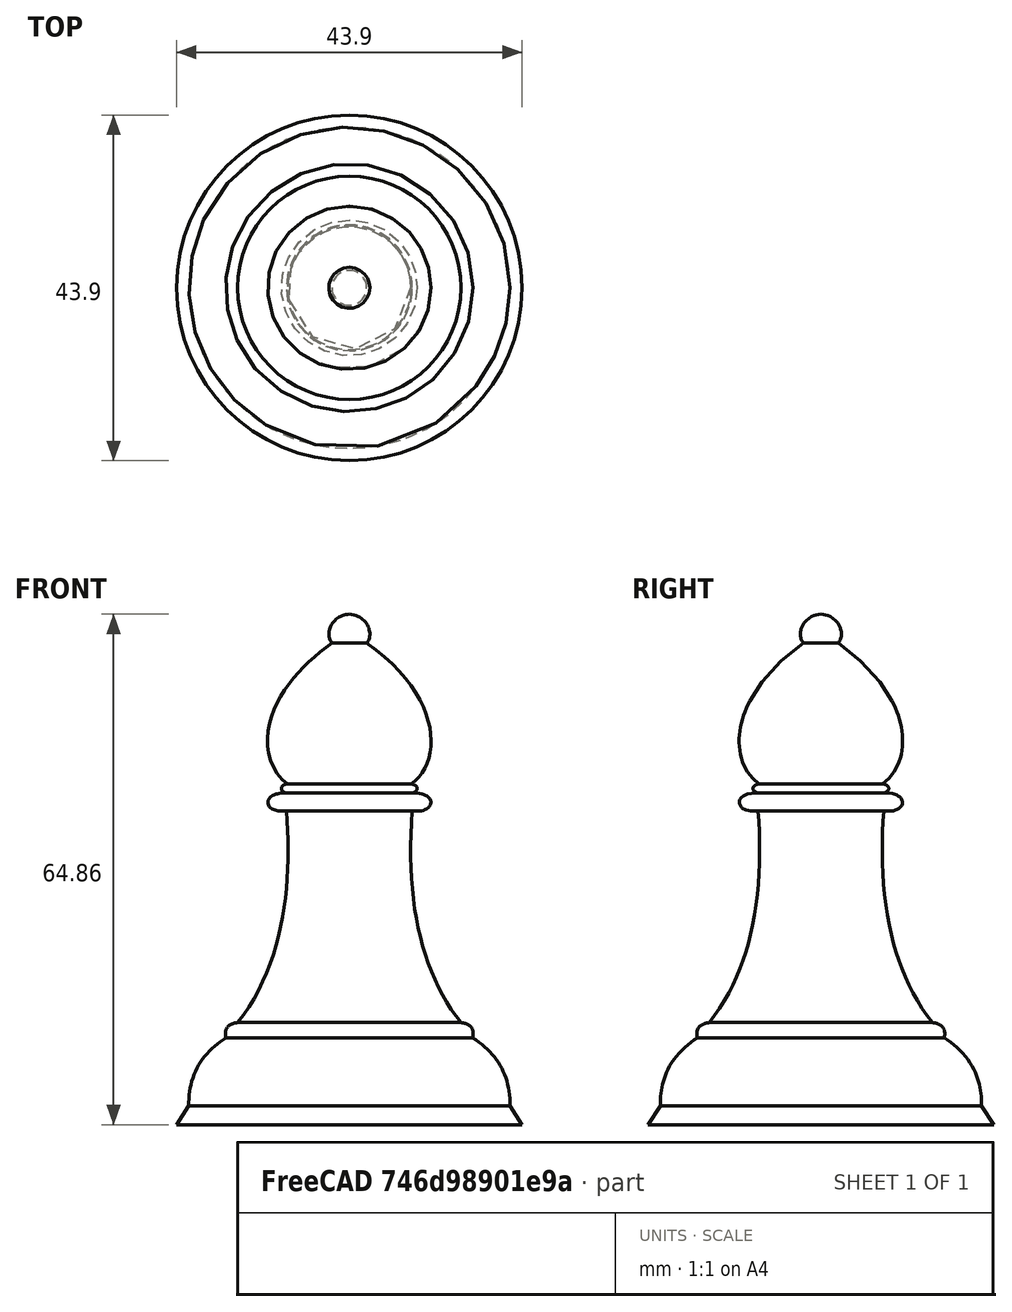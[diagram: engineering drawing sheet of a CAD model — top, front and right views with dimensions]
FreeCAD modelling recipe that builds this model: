
FCSTD DOCUMENT  (FreeCAD 0.20R29177 +426 (Git))
Label: alfil
License: Creative Commons Attribution-ShareAlike
LicenseURL: http://creativecommons.org/licenses/by-sa/4.0/
objects: Sketcher::SketchObject×1, Part::Revolution×1
note: 2 computed .brp shape members not serialized (recipe doc carries the construction recipe); baked Part::Feature solids carry a one-line shape summary decoded from their .brp

FEATURE [Sketcher::SketchObject] Sketch
  FullyConstrained = false
  Placement = pos=(0,0,0) rot=(1,0,0;1.5708rad)
  sketch-geometry (49):
    g0: LineSegment StartX=0 StartY=0 StartZ=0 EndX=21.9512 EndY=0 EndZ=0
    g1: LineSegment StartX=21.9512 StartY=0 StartZ=0 EndX=20.4013 EndY=2.40979 EndZ=0
    g2: Circle CenterX=20.4013 CenterY=2.40979 CenterZ=0 NormalX=0 NormalY=0 NormalZ=1 AngleXU=0 Radius=1
    g3: Circle CenterX=20.4986 CenterY=7.95886 CenterZ=0 NormalX=0 NormalY=0 NormalZ=1 AngleXU=0 Radius=1
    g4: Circle CenterX=15.6707 CenterY=11.0375 CenterZ=0 NormalX=0 NormalY=0 NormalZ=1 AngleXU=0 Radius=1
    g5: BSplineCurve PolesCount=3 KnotsCount=2 Degree=2 IsPeriodic=0
    g6: GeomPoint X=20.4013 Y=2.40979 Z=0
    g7: GeomPoint X=15.6707 Y=11.0375 Z=0
    g8: Circle CenterX=15.6707 CenterY=11.0375 CenterZ=0 NormalX=0 NormalY=0 NormalZ=1 AngleXU=0 Radius=1
    g9: Circle CenterX=16.0644 CenterY=12.7435 CenterZ=0 NormalX=0 NormalY=0 NormalZ=1 AngleXU=0 Radius=1
    g10: Circle CenterX=14.1834 CenterY=12.9622 CenterZ=0 NormalX=0 NormalY=0 NormalZ=1 AngleXU=0 Radius=1
    g11: BSplineCurve PolesCount=3 KnotsCount=2 Degree=2 IsPeriodic=0
    g12: GeomPoint X=15.6707 Y=11.0375 Z=0
    g13: GeomPoint X=14.1834 Y=12.9622 Z=0
    g14: Circle CenterX=14.1834 CenterY=12.9622 CenterZ=0 NormalX=0 NormalY=0 NormalZ=1 AngleXU=0 Radius=1
    g15: Circle CenterX=6.6662 CenterY=22.465 CenterZ=0 NormalX=0 NormalY=0 NormalZ=1 AngleXU=0 Radius=1
    g16: Circle CenterX=7.98136 CenterY=39.8756 CenterZ=0 NormalX=0 NormalY=0 NormalZ=1 AngleXU=0 Radius=1
    g17: BSplineCurve PolesCount=3 KnotsCount=2 Degree=2 IsPeriodic=0
    g18: GeomPoint X=14.1834 Y=12.9622 Z=0
    g19: GeomPoint X=7.98136 Y=39.8756 Z=0
    g20-g23: Circle x4 (B-spline internal-alignment scaffolding for g24; pole/knot coordinates omitted)
    g24: BSplineCurve PolesCount=4 KnotsCount=2 Degree=3 IsPeriodic=0
    g25: GeomPoint X=7.98136 Y=39.8756 Z=0
    g26: GeomPoint X=7.9451 Y=42.1219 Z=0
    g27: Circle CenterX=7.9451 CenterY=42.1219 CenterZ=0 NormalX=0 NormalY=0 NormalZ=1 AngleXU=0 Radius=1
    g28: Circle CenterX=9.0659 CenterY=42.3703 CenterZ=0 NormalX=0 NormalY=0 NormalZ=1 AngleXU=0 Radius=1
    g29: Circle CenterX=8.64352 CenterY=43.2767 CenterZ=0 NormalX=0 NormalY=0 NormalZ=1 AngleXU=0 Radius=1
    g30: Circle CenterX=7.84367 CenterY=43.2664 CenterZ=0 NormalX=0 NormalY=0 NormalZ=1 AngleXU=0 Radius=1
    g31: BSplineCurve PolesCount=4 KnotsCount=2 Degree=3 IsPeriodic=0
    g32: GeomPoint X=7.9451 Y=42.1219 Z=0
    g33: GeomPoint X=7.84367 Y=43.2664 Z=0
    g34: Circle CenterX=7.84367 CenterY=43.2664 CenterZ=0 NormalX=0 NormalY=0 NormalZ=1 AngleXU=0 Radius=1
    g35: Circle CenterX=12.0104 CenterY=46.2983 CenterZ=0 NormalX=0 NormalY=0 NormalZ=1 AngleXU=0 Radius=1
    g36: Circle CenterX=11.6605 CenterY=54.5658 CenterZ=0 NormalX=0 NormalY=0 NormalZ=1 AngleXU=0 Radius=1
    g37: Circle CenterX=2.21194 CenterY=61.171 CenterZ=0 NormalX=0 NormalY=0 NormalZ=1 AngleXU=0 Radius=1
    g38: BSplineCurve PolesCount=4 KnotsCount=2 Degree=3 IsPeriodic=0
    g39: GeomPoint X=7.84367 Y=43.2664 Z=0
    g40: GeomPoint X=2.21194 Y=61.171 Z=0
    g41-g44: Circle x4 (B-spline internal-alignment scaffolding for g45; pole/knot coordinates omitted)
    g45: BSplineCurve PolesCount=4 KnotsCount=2 Degree=3 IsPeriodic=0
    g46: GeomPoint X=2.21194 Y=61.171 Z=0
    g47: GeomPoint X=0 Y=64.8609 Z=0
    g48: LineSegment StartX=0 StartY=64.8609 StartZ=0 EndX=0 EndY=0 EndZ=0
  constraints (44):
    c: PointOnObject(g0,g-1)
    c: Weight(g2) = 1
    c: Equal(g2,g3)
    c: Equal(g2,g4)
    c: InternalAlignment(g2,g5)
    c: InternalAlignment(g3,g5)
    c: InternalAlignment(g4,g5)
    c: InternalAlignment(g6,g5)
    c: InternalAlignment(g7,g5)
    c: Weight(g8) = 1
    c: Equal(g8,g9)
    c: Equal(g8,g10)
    c: InternalAlignment(g8,g11)
    c: InternalAlignment(g9,g11)
    c: InternalAlignment(g10,g11)
    c: InternalAlignment(g12,g11)
    c: InternalAlignment(g13,g11)
    c: Weight(g14) = 1
    c: Equal(g14,g15)
    c: Equal(g14,g16)
    c: InternalAlignment(g14,g17)
    c: InternalAlignment(g15,g17)
    c: InternalAlignment(g16,g17)
    c: InternalAlignment(g18,g17)
    c: InternalAlignment(g19,g17)
    c: Weight(g20) = 1
    c: Equal(g20,g21)
    c: Equal(g20,g22)
    c: Equal(g20,g23)
    c: InternalAlignment(g20-g23 -> g24) x4
    c: InternalAlignment(g25,g24)
    c: InternalAlignment(g26,g24)
    c: Weight(g27) = 1
    c: Equal(g27,g28)
    c: Equal(g27,g29)
    c: PointOnObject(g29,g28)
    c: Equal(g27,g30)
    c: InternalAlignment(g27,g31)
    c: InternalAlignment(g28,g31)
    c: InternalAlignment(g29,g31)
    c: InternalAlignment(g41-g44 -> g45) x4
    c: InternalAlignment(g46,g45)
    c: InternalAlignment(g47,g45)
    c: Horizontal(g0)
FEATURE [Part::Revolution] Revolve
  Angle = 360
  Axis = (0,0,1)
  Base = (0,0,0)
  FaceMakerClass = Part::FaceMakerBullseye
  Solid = true
  Source = -> Sketch
  Symmetric = false
